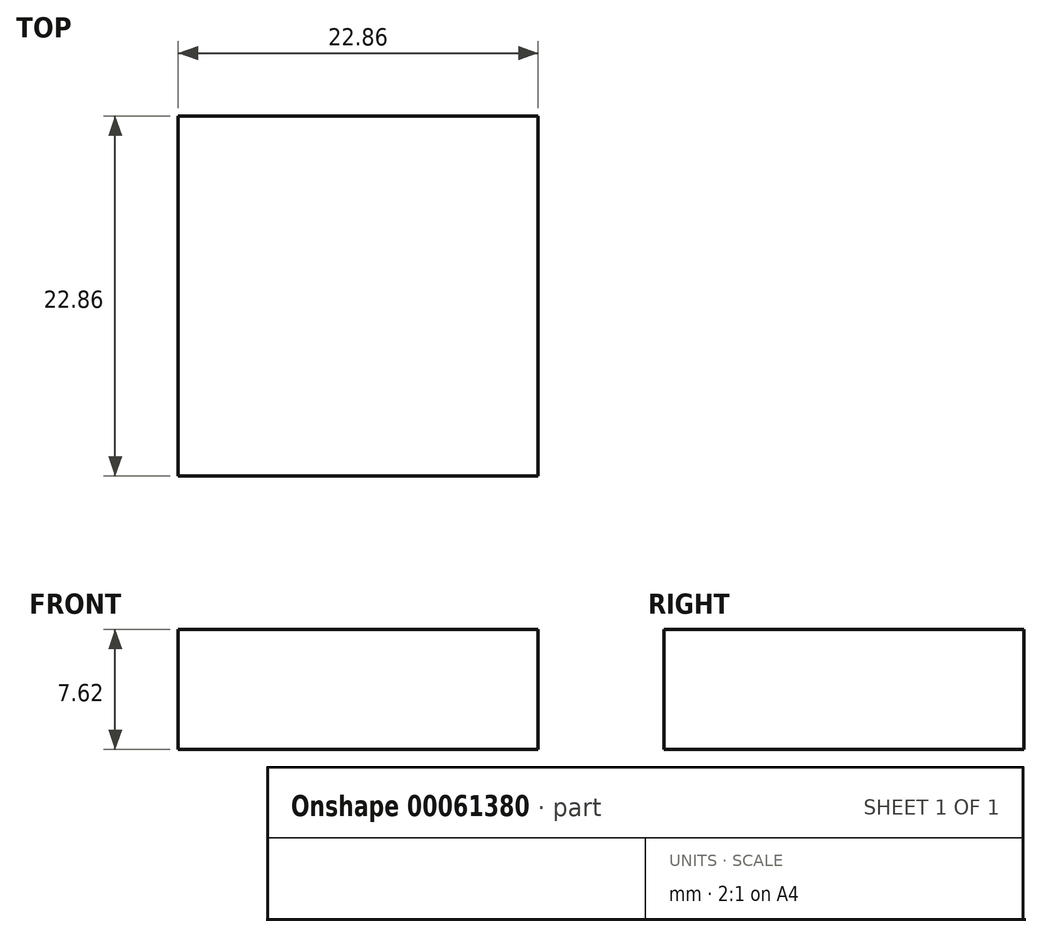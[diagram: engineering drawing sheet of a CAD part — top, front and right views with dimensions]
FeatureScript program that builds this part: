
annotation { "Feature Type Name" : "Feature", "Feature Type Description" : "" }
export const myFeature = defineFeature(function(context is Context, id is Id, definition is map)
    precondition{}
    {
        {
            var Q0;
            Q0=qCreatedBy(makeId("Top.planeOp"),FACE);
            var sketch = newSketch(context, id + "F0", { "sketchPlane" : qUnion([Q0])});
            skLineSegment(sketch, "E0.rect.bottom", {"start": v(11.43, 11.43) * mm, "end": v(-11.43, 11.43) * mm});
            skLineSegment(sketch, "E0.rect.top", {"start": v(11.43, -11.43) * mm, "end": v(-11.43, -11.43) * mm});
            skLineSegment(sketch, "E0.rect.left", {"start": v(11.43, 11.43) * mm, "end": v(11.43, -11.43) * mm});
            skLineSegment(sketch, "E0.rect.right", {"start": v(-11.43, 11.43) * mm, "end": v(-11.43, -11.43) * mm});
            skPoint(sketch, "E0.rect.middle", {"position": v(0, 0) * mm});
            skSolve(sketch);
        }
        {
            var Q0;
            Q0 = qSketchRegion(id + "F0", true);
            extrude(context, id + "F1", {"entities" : qUnion([Q0]), "depth" : 7.62 * mm});
        }
    });
